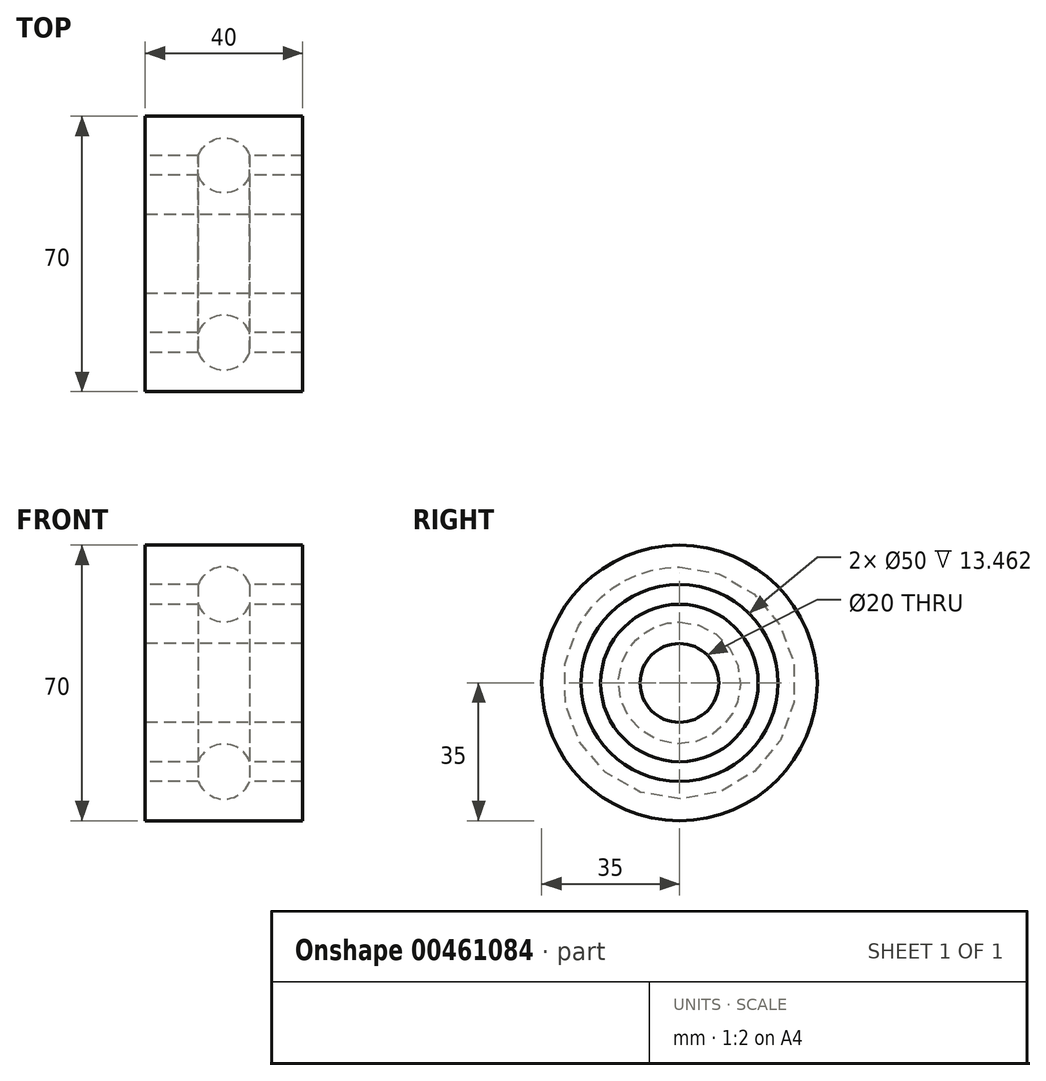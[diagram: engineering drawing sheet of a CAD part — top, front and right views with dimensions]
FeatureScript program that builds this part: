
annotation { "Feature Type Name" : "Feature", "Feature Type Description" : "" }
export const myFeature = defineFeature(function(context is Context, id is Id, definition is map)
    precondition{}
    {
        {
            var Q0;
            Q0=qCreatedBy(makeId("Front.planeOp"),FACE);
            var sketch = newSketch(context, id + "F0", { "sketchPlane" : qUnion([Q0])});
            skLineSegment(sketch, "E0", {"start": v(0, 0) * mm, "end": v(0, 20) * mm, "construction": true});
            skLineSegment(sketch, "E1", {"start": v(0, 35) * mm, "end": v(20, 35) * mm});
            skLineSegment(sketch, "E2", {"start": v(20, 35) * mm, "end": v(20, 25) * mm});
            skLineSegment(sketch, "E3", {"start": v(20, 25) * mm, "end": v(6.54, 25) * mm});
            skLineSegment(sketch, "E4", {"start": v(6.54, 20) * mm, "end": v(20, 20) * mm});
            skLineSegment(sketch, "E5", {"start": v(20, 20) * mm, "end": v(20, 10) * mm});
            skLineSegment(sketch, "E6", {"start": v(20, 10) * mm, "end": v(0, 10) * mm});
            skLineSegment(sketch, "E7", {"start": v(0, 0) * mm, "end": v(45.77, 0) * mm, "construction": true});
            skArc(sketch, "E8", {"start": v(0, 29.5) * mm, "mid": v(3.97, 28.27) * mm, "end": v(6.54, 25) * mm});
            skLineSegment(sketch, "E9", {"start": v(0, 35) * mm, "end": v(0, 29.5) * mm});
            skLineSegment(sketch, "E10", {"start": v(0, 15.5) * mm, "end": v(0, 10) * mm});
            skArc(sketch, "E11.trimOffspring", {"start": v(6.54, 20) * mm, "mid": v(3.97, 16.73) * mm, "end": v(0, 15.5) * mm});
            skLineSegment(sketch, "E12.trimOffspring", {"start": v(0, 25) * mm, "end": v(0, 43.81) * mm, "construction": true});
            skLineSegment(sketch, "E13.MirrorCS", {"start": v(0, 35) * mm, "end": v(-20, 35) * mm});
            skLineSegment(sketch, "E14.MirrorCS", {"start": v(-20, 35) * mm, "end": v(-20, 25) * mm});
            skLineSegment(sketch, "E15.MirrorCS", {"start": v(-20, 25) * mm, "end": v(-6.54, 25) * mm});
            skArc(sketch, "E16.MirrorCS", {"start": v(0, 29.5) * mm, "mid": v(-3.97, 28.27) * mm, "end": v(-6.54, 25) * mm});
            skArc(sketch, "E17.MirrorCS", {"start": v(-6.54, 20) * mm, "mid": v(-3.97, 16.73) * mm, "end": v(0, 15.5) * mm});
            skLineSegment(sketch, "E18.MirrorCS", {"start": v(-6.54, 20) * mm, "end": v(-20, 20) * mm});
            skLineSegment(sketch, "E19.MirrorCS", {"start": v(-20, 20) * mm, "end": v(-20, 10) * mm});
            skLineSegment(sketch, "E20.MirrorCS", {"start": v(-20, 10) * mm, "end": v(0, 10) * mm});
            skSolve(sketch);
        }
        {
            var Q0;
            Q0 = qSketchRegion(id + "F0", true);
            var Q1;
            Q1=sQuery(id+"F0.wireOp",EDGE,"E7");
            revolve(context, id + "F1", {"entities" : qUnion([Q0]), "axis" : qUnion([Q1]), "revolveType" : RevolveType.FULL});
        }
    });
